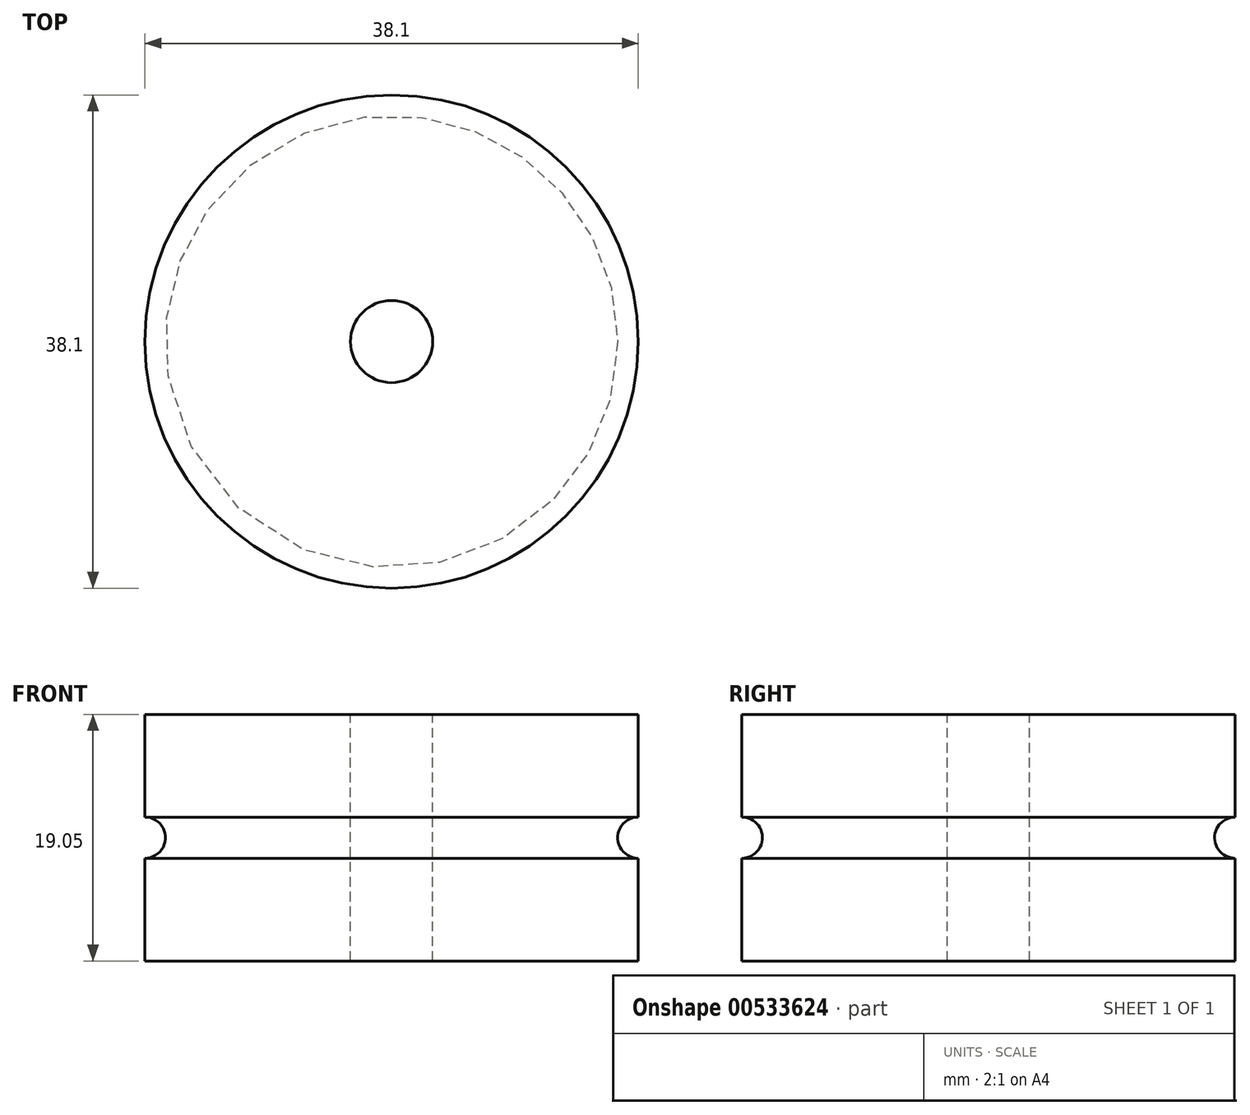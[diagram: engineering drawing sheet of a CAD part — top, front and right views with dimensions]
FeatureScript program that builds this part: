
annotation { "Feature Type Name" : "Feature", "Feature Type Description" : "" }
export const myFeature = defineFeature(function(context is Context, id is Id, definition is map)
    precondition{}
    {
        {
            var Q0;
            Q0=qCreatedBy(makeId("Front.planeOp"),FACE);
            var sketch = newSketch(context, id + "F0", { "sketchPlane" : qUnion([Q0])});
            skLineSegment(sketch, "E0.bottom", {"start": v(0, 0) * mm, "end": v(-19.05, 0) * mm});
            skLineSegment(sketch, "E0.top", {"start": v(0, -19.05) * mm, "end": v(-19.05, -19.05) * mm});
            skLineSegment(sketch, "E0.left", {"start": v(0, 0) * mm, "end": v(0, -19.05) * mm});
            skLineSegment(sketch, "E0.right", {"start": v(-19.05, 0) * mm, "end": v(-19.05, -19.05) * mm});
            skCircle(sketch, "E1", {"center": v(-19.05, -9.53) * mm, "radius": 1.59 * mm});
            skSolve(sketch);
        }
        {
            var Q0;
            {var subQ1=sQuery(id+"F0.wireOp",EDGE,"E0.bottom");Q0=makeQuery(id+"F0.imprint","IMPRINT",FACE,{"disambiguationData":[TD([[makeQuery(id+"F0.imprint","IMPRINT",EDGE,{"derivedFrom":subQ1}),1.0]])]});}
            var Q1;
            Q1=sQuery(id+"F0.wireOp",EDGE,"E0.left");
            revolve(context, id + "F1", {"entities" : qUnion([Q0]), "axis" : qUnion([Q1]), "revolveType" : RevolveType.FULL});
        }
        {
            var Q0;
            Q0=makeQuery(id+"F1.opRevolve","SWEPT_FACE",FACE,{"disambiguationData":[OSD([sQuery(id+"F0.wireOp",EDGE,"E0.bottom")])]});
            var sketch = newSketch(context, id + "F2", { "sketchPlane" : qUnion([Q0])});
            skCircle(sketch, "E2", {"center": v(0, 0) * mm, "radius": 3.18 * mm});
            skSolve(sketch);
        }
        {
            var Q0;
            Q0=makeQuery(id+"F2.imprint","IMPRINT",FACE,{"disambiguationData":[TD([[makeQuery(id+"F2.imprint","IMPRINT",EDGE,{"derivedFrom":sQuery(id+"F2.wireOp",EDGE,"E2")}),1.0]])]});
            extrude(context, id + "F3", {"entities" : qUnion([Q0]), "operationType" : NewBodyOperationType.REMOVE, "oppositeDirection" : true, "depth" : 25.4 * mm, "offsetDistance" : 25.4 * mm});
        }
    });
